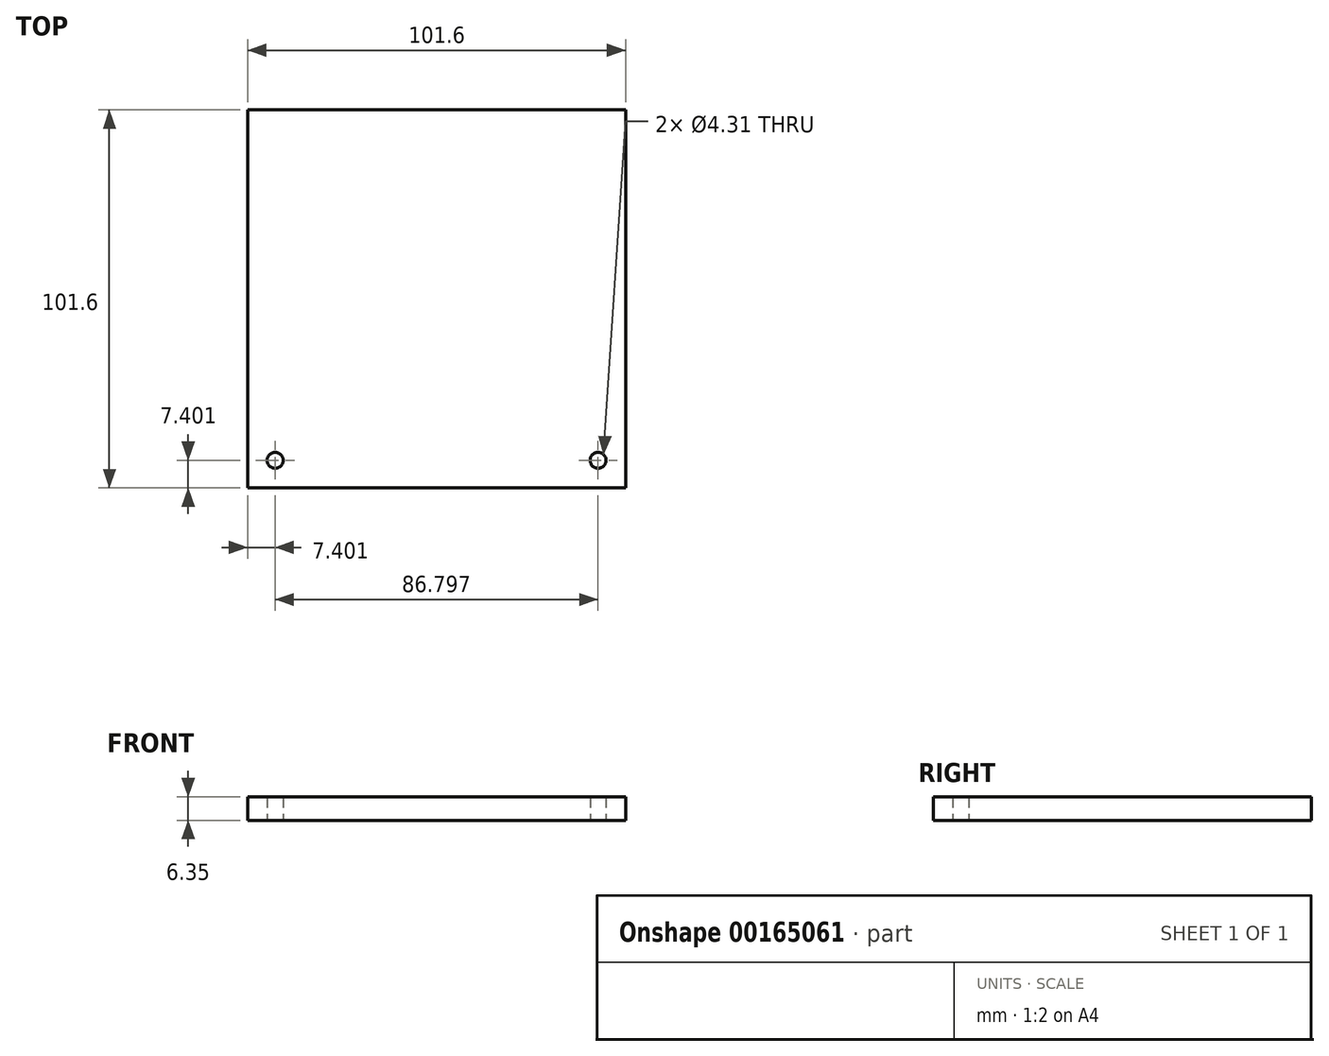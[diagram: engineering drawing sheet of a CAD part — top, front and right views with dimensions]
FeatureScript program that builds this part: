
annotation { "Feature Type Name" : "Feature", "Feature Type Description" : "" }
export const myFeature = defineFeature(function(context is Context, id is Id, definition is map)
    precondition{}
    {
        {
            var Q0;
            Q0=qCreatedBy(makeId("Top.planeOp"),FACE);
            var sketch = newSketch(context, id + "F0", { "sketchPlane" : qUnion([Q0])});
            skLineSegment(sketch, "E0.bottom", {"start": v(0, 0) * mm, "end": v(-101.6, 0) * mm});
            skLineSegment(sketch, "E0.top", {"start": v(0, -101.6) * mm, "end": v(-101.6, -101.6) * mm});
            skLineSegment(sketch, "E0.left", {"start": v(0, 0) * mm, "end": v(0, -101.6) * mm});
            skLineSegment(sketch, "E0.right", {"start": v(-101.6, 0) * mm, "end": v(-101.6, -101.6) * mm});
            skLineSegment(sketch, "E1", {"start": v(-50.8, -101.6) * mm, "end": v(-50.8, -94.2) * mm, "construction": true});
            skLineSegment(sketch, "E2", {"start": v(-94.2, -94.2) * mm, "end": v(-7.4, -94.2) * mm, "construction": true});
            skLineSegment(sketch, "E3", {"start": v(-7.4, -94.2) * mm, "end": v(0, -94.2) * mm, "construction": true});
            skCircle(sketch, "E4", {"center": v(-94.2, -94.2) * mm, "radius": 2.15 * mm});
            skCircle(sketch, "E5", {"center": v(-7.4, -94.2) * mm, "radius": 2.15 * mm});
            skSolve(sketch);
        }
        {
            var Q0;
            Q0 = qSketchRegion(id + "F0", true);
            extrude(context, id + "F1", {"entities" : qUnion([Q0]), "depth" : 6.35 * mm});
        }
    });
